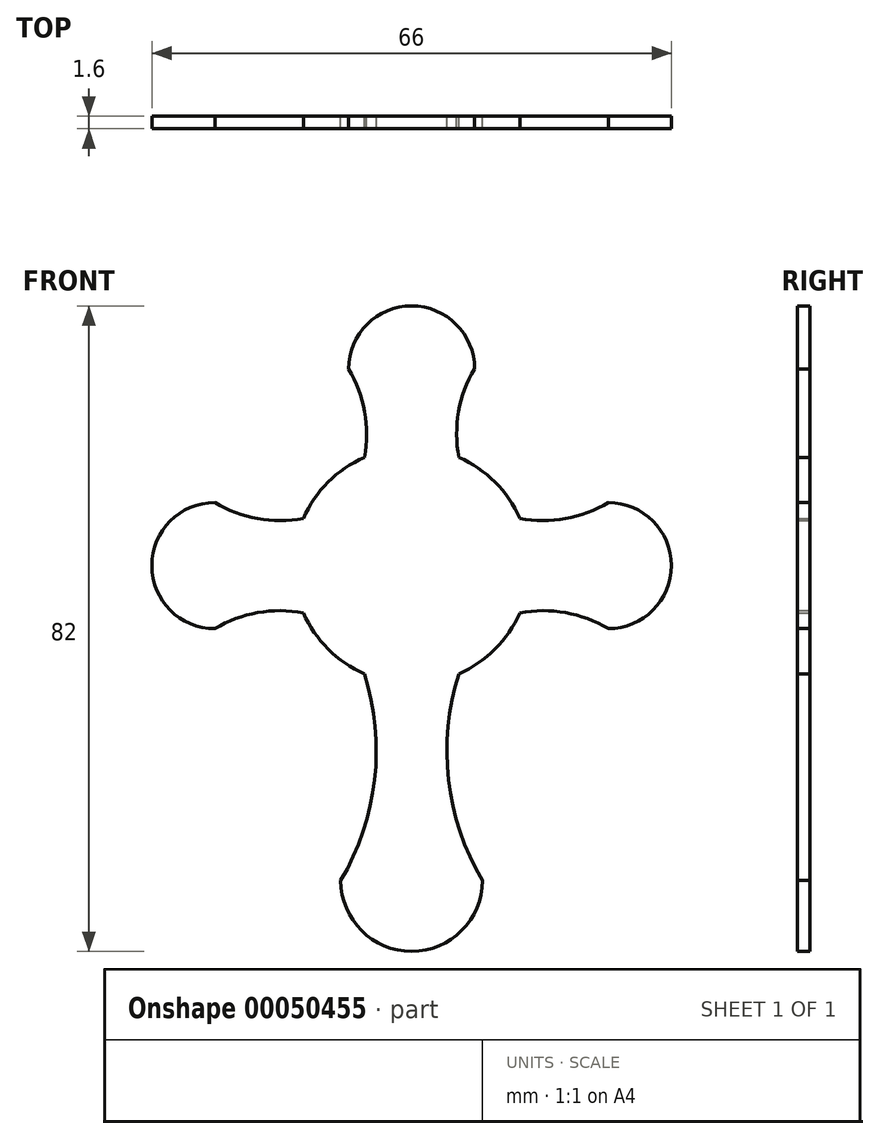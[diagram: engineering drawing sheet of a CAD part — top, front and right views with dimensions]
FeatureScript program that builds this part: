
annotation { "Feature Type Name" : "Feature", "Feature Type Description" : "" }
export const myFeature = defineFeature(function(context is Context, id is Id, definition is map)
    precondition{}
    {
        {
            var Q0;
            Q0=qCreatedBy(makeId("Front.planeOp"),FACE);
            var sketch = newSketch(context, id + "F0", { "sketchPlane" : qUnion([Q0])});
            skArc(sketch, "E0", {"start": v(6, -13.75) * mm, "mid": v(10.6, -10.6) * mm, "end": v(13.75, -6) * mm});
            skArc(sketch, "E1", {"start": v(8, 25) * mm, "mid": v(0, 33) * mm, "end": v(-8, 25) * mm});
            skArc(sketch, "E2", {"start": v(25, -8) * mm, "mid": v(33, 0) * mm, "end": v(25, 8) * mm});
            skArc(sketch, "E3", {"start": v(-25, 8) * mm, "mid": v(-33, 0) * mm, "end": v(-25, -8) * mm});
            skArc(sketch, "E4", {"start": v(-9, -40) * mm, "mid": v(0, -49) * mm, "end": v(9, -40) * mm});
            skPoint(sketch, "E5.bottom.start.orphan", {"position": v(-6, 25) * mm});
            skPoint(sketch, "E6.orphan", {"position": v(-25, 6) * mm});
            skPoint(sketch, "E7.orphan", {"position": v(25, -6) * mm});
            skPoint(sketch, "E8.orphan", {"position": v(6, -40) * mm});
            skArc(sketch, "E9.trimOffspring", {"start": v(13.75, 6) * mm, "mid": v(10.6, 10.6) * mm, "end": v(6, 13.75) * mm});
            skArc(sketch, "E10.trimOffspring", {"start": v(-13.75, -6) * mm, "mid": v(-10.6, -10.6) * mm, "end": v(-6, -13.75) * mm});
            skArc(sketch, "E11.trimOffspring", {"start": v(-6, 13.75) * mm, "mid": v(-10.6, 10.6) * mm, "end": v(-13.75, 6) * mm});
            skLineSegment(sketch, "E12", {"start": v(38.39, 25) * mm, "end": v(-36.89, 25) * mm, "construction": true});
            skArc(sketch, "E13", {"start": v(-6, 13.75) * mm, "mid": v(-5.97, 19.56) * mm, "end": v(-8, 25) * mm});
            skArc(sketch, "E14", {"start": v(8, 25) * mm, "mid": v(5.97, 19.56) * mm, "end": v(6, 13.75) * mm});
            skLineSegment(sketch, "E15", {"start": v(-25, 16.73) * mm, "end": v(-25, -15.17) * mm, "construction": true});
            skLineSegment(sketch, "E16", {"start": v(25, 12.97) * mm, "end": v(25, -16.63) * mm, "construction": true});
            skLineSegment(sketch, "E17", {"start": v(-23.73, -40) * mm, "end": v(24.87, -40) * mm, "construction": true});
            skArc(sketch, "E18", {"start": v(-13.75, -6) * mm, "mid": v(-19.56, -5.97) * mm, "end": v(-25, -8) * mm});
            skArc(sketch, "E19", {"start": v(-25, 8) * mm, "mid": v(-19.56, 5.97) * mm, "end": v(-13.75, 6) * mm});
            skArc(sketch, "E20", {"start": v(25, -8) * mm, "mid": v(19.56, -5.97) * mm, "end": v(13.75, -6) * mm});
            skArc(sketch, "E21", {"start": v(13.75, 6) * mm, "mid": v(19.56, 5.97) * mm, "end": v(25, 8) * mm});
            skArc(sketch, "E22", {"start": v(-9, -40) * mm, "mid": v(-4.7, -27.2) * mm, "end": v(-6, -13.75) * mm});
            skArc(sketch, "E23", {"start": v(6, -13.75) * mm, "mid": v(4.7, -27.2) * mm, "end": v(9, -40) * mm});
            skSolve(sketch);
        }
        {
            var Q0;
            Q0 = qSketchRegion(id + "F0", true);
            extrude(context, id + "F1", {"entities" : qUnion([Q0]), "depth" : 1.6 * mm});
        }
    });
